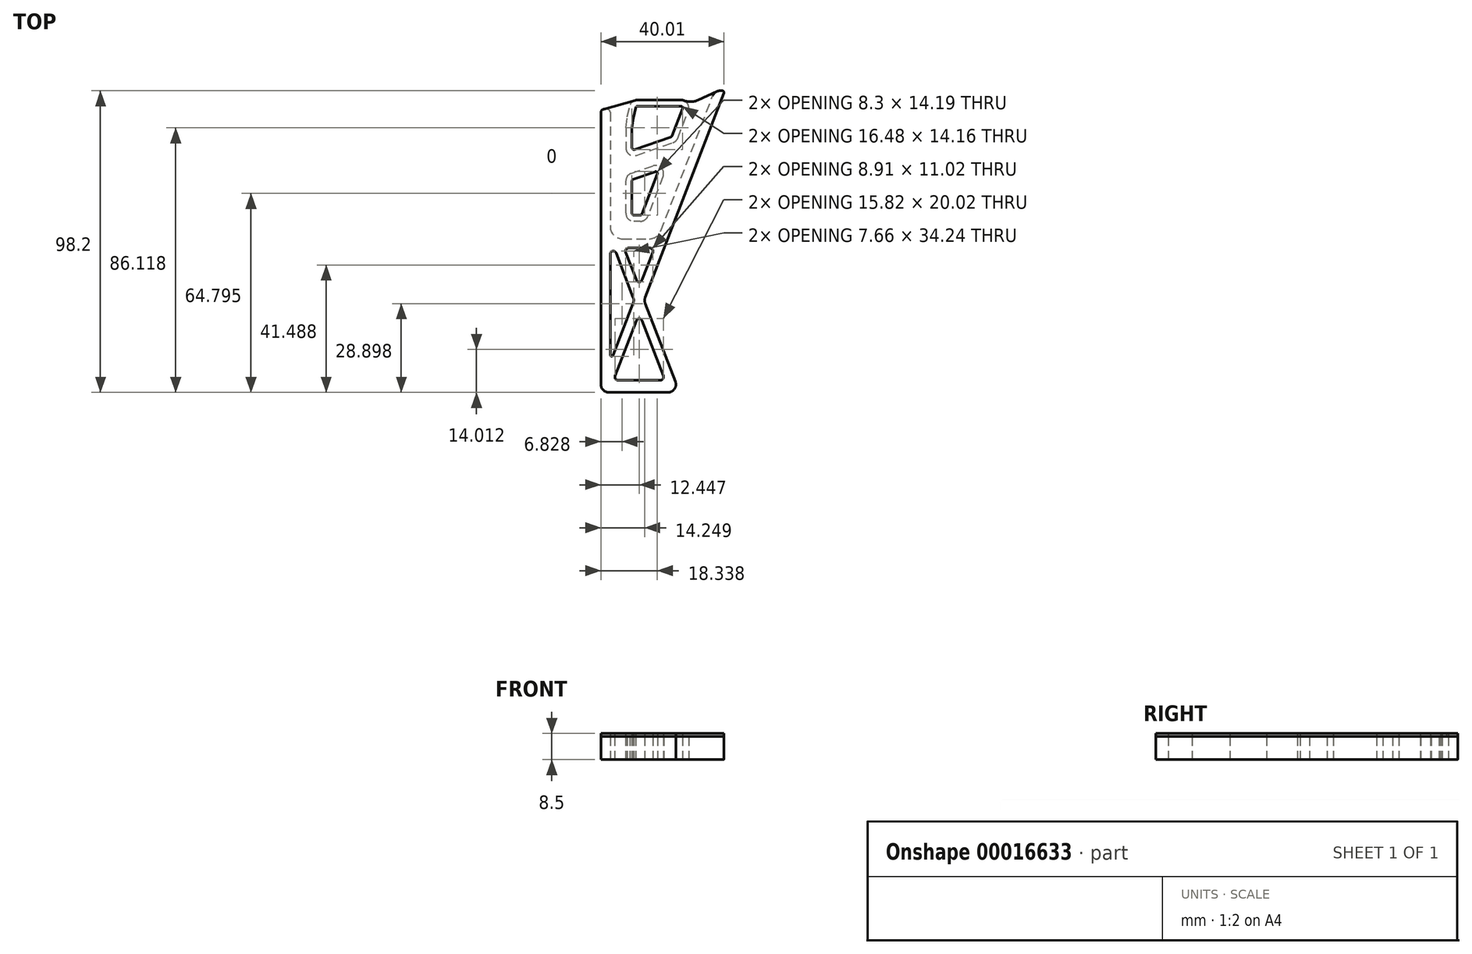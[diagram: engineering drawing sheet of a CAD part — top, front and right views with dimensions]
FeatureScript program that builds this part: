
annotation { "Feature Type Name" : "Feature", "Feature Type Description" : "" }
export const myFeature = defineFeature(function(context is Context, id is Id, definition is map)
    precondition{}
    {
        {
            var Q0;
            Q0=qCreatedBy(makeId("Top.planeOp"),FACE);
            var sketch = newSketch(context, id + "F0", { "sketchPlane" : qUnion([Q0])});
            skLineSegment(sketch, "E0", {"start": v(0, 2.6) * mm, "end": v(0, 13.15) * mm});
            skLineSegment(sketch, "E1", {"start": v(1.75, 15.6) * mm, "end": v(8.85, 18.05) * mm});
            skLineSegment(sketch, "E2", {"start": v(12.13, 14.66) * mm, "end": v(7.14, 1.67) * mm});
            skLineSegment(sketch, "E3", {"start": v(4.71, 0) * mm, "end": v(2.6, 0) * mm});
            skPoint(sketch, "E4.visualSharp", {"position": v(14.12, 19.86) * mm});
            skArc(sketch, "E4.filletArc", {"start": v(12.13, 14.66) * mm, "mid": v(11.57, 17.4) * mm, "end": v(8.85, 18.05) * mm});
            skPoint(sketch, "E5.visualSharp", {"position": v(0, 15) * mm});
            skArc(sketch, "E5.filletArc", {"start": v(1.75, 15.6) * mm, "mid": v(0.48, 14.66) * mm, "end": v(0, 13.15) * mm});
            skPoint(sketch, "E6.visualSharp", {"position": v(0, 0) * mm});
            skArc(sketch, "E6.filletArc", {"start": v(0, 2.6) * mm, "mid": v(0.76, 0.76) * mm, "end": v(2.6, 0) * mm});
            skPoint(sketch, "E7.visualSharp", {"position": v(6.5, 0) * mm});
            skArc(sketch, "E7.filletArc", {"start": v(4.71, 0) * mm, "mid": v(6.19, 0.46) * mm, "end": v(7.14, 1.67) * mm});
            skLineSegment(sketch, "E8", {"start": v(0, 30.5) * mm, "end": v(0, 23.93) * mm});
            skLineSegment(sketch, "E9", {"start": v(3.45, 21.47) * mm, "end": v(15.32, 25.56) * mm});
            skLineSegment(sketch, "E10", {"start": v(16.9, 27.09) * mm, "end": v(20.3, 35.97) * mm});
            skLineSegment(sketch, "E11", {"start": v(17.88, 39.5) * mm, "end": v(3.83, 39.5) * mm});
            skLineSegment(sketch, "E12", {"start": v(7.14, 1.67) * mm, "end": v(22.81, 42.5) * mm, "construction": true});
            skLineSegment(sketch, "E13", {"start": v(0, 2.6) * mm, "end": v(0, 43.18) * mm, "construction": true});
            skPoint(sketch, "E14.visualSharp", {"position": v(0, 20.29) * mm});
            skArc(sketch, "E14.filletArc", {"start": v(0, 23.93) * mm, "mid": v(1.1, 21.82) * mm, "end": v(3.45, 21.47) * mm});
            skPoint(sketch, "E15.visualSharp", {"position": v(16.46, 25.96) * mm});
            skArc(sketch, "E15.filletArc", {"start": v(15.32, 25.56) * mm, "mid": v(16.28, 26.15) * mm, "end": v(16.9, 27.09) * mm});
            skLineSegment(sketch, "E16", {"start": v(0, 30.5) * mm, "end": v(1.27, 37.37) * mm, "construction": true});
            skPoint(sketch, "E17.visualSharp", {"position": v(21.66, 39.5) * mm});
            skArc(sketch, "E17.filletArc", {"start": v(20.3, 35.97) * mm, "mid": v(20.02, 38.37) * mm, "end": v(17.88, 39.5) * mm});
            skPoint(sketch, "E18.visualSharp", {"position": v(1.66, 39.5) * mm});
            skArc(sketch, "E18.filletArc", {"start": v(3.83, 39.5) * mm, "mid": v(2.16, 38.9) * mm, "end": v(1.27, 37.37) * mm});
            skLineSegment(sketch, "E19", {"start": v(-5.1, 35.5) * mm, "end": v(-5.1, -1.7) * mm});
            skLineSegment(sketch, "E20", {"start": v(-1.1, -5.7) * mm, "end": v(7.67, -5.7) * mm});
            skLineSegment(sketch, "E21", {"start": v(11.4, -3.13) * mm, "end": v(28.28, 40.83) * mm});
            skLineSegment(sketch, "E22", {"start": v(-27.96, 39.5) * mm, "end": v(46.58, 39.5) * mm, "construction": true});
            skLineSegment(sketch, "E23", {"start": v(30.7, 42.5) * mm, "end": v(31.4, 42.5) * mm});
            skPoint(sketch, "E24.visualSharp", {"position": v(28.92, 42.5) * mm});
            skArc(sketch, "E24.filletArc", {"start": v(30.7, 42.5) * mm, "mid": v(29.23, 42.04) * mm, "end": v(28.28, 40.83) * mm});
            skLineSegment(sketch, "E25", {"start": v(-6.1, 36.5) * mm, "end": v(-7.1, 36.5) * mm});
            skLineSegment(sketch, "E26", {"start": v(-8.1, 35.5) * mm, "end": v(-8.1, -53.1) * mm});
            skLineSegment(sketch, "E27", {"start": v(6.31, -24.77) * mm, "end": v(31.87, 41.82) * mm});
            skPoint(sketch, "E28.visualSharp", {"position": v(-8.1, 36.5) * mm});
            skArc(sketch, "E28.filletArc", {"start": v(-7.1, 36.5) * mm, "mid": v(-7.8, 36.2) * mm, "end": v(-8.1, 35.5) * mm});
            skPoint(sketch, "E29.visualSharp", {"position": v(-5.1, 36.5) * mm});
            skArc(sketch, "E29.filletArc", {"start": v(-5.1, 35.5) * mm, "mid": v(-5.4, 36.2) * mm, "end": v(-6.1, 36.5) * mm});
            skPoint(sketch, "E30.visualSharp", {"position": v(32.13, 42.5) * mm});
            skArc(sketch, "E30.filletArc", {"start": v(31.87, 41.82) * mm, "mid": v(31.82, 42.28) * mm, "end": v(31.4, 42.5) * mm});
            skPoint(sketch, "E31.visualSharp", {"position": v(-5.1, -5.7) * mm});
            skArc(sketch, "E31.filletArc", {"start": v(-5.1, -1.7) * mm, "mid": v(-3.93, -4.53) * mm, "end": v(-1.1, -5.7) * mm});
            skPoint(sketch, "E32.visualSharp", {"position": v(10.42, -5.7) * mm});
            skArc(sketch, "E32.filletArc", {"start": v(7.67, -5.7) * mm, "mid": v(9.93, -5) * mm, "end": v(11.4, -3.13) * mm});
            skLineSegment(sketch, "E33", {"start": v(0, 30.5) * mm, "end": v(0.44, 33.97) * mm});
            skLineSegment(sketch, "E34", {"start": v(0.44, 33.97) * mm, "end": v(1.27, 37.37) * mm});
            skLineSegment(sketch, "E35", {"start": v(-31.23, -55.7) * mm, "end": v(37.12, -55.7) * mm, "construction": true});
            skLineSegment(sketch, "E36", {"start": v(16.11, -52.17) * mm, "end": v(6.31, -26.63) * mm});
            skLineSegment(sketch, "E37", {"start": v(13.69, -55.7) * mm, "end": v(-5.5, -55.7) * mm});
            skLineSegment(sketch, "E38", {"start": v(3.41, -32.32) * mm, "end": v(-3.5, -50.34) * mm});
            skLineSegment(sketch, "E39", {"start": v(-2.57, -51.7) * mm, "end": v(11.27, -51.7) * mm});
            skLineSegment(sketch, "E40", {"start": v(12.2, -50.34) * mm, "end": v(5.28, -32.32) * mm});
            skLineSegment(sketch, "E41", {"start": v(-0.05, -10.06) * mm, "end": v(3.41, -19.08) * mm});
            skLineSegment(sketch, "E42", {"start": v(5.28, -19.08) * mm, "end": v(8.74, -10.06) * mm});
            skLineSegment(sketch, "E43", {"start": v(7.81, -8.7) * mm, "end": v(0.88, -8.7) * mm});
            skLineSegment(sketch, "E44", {"start": v(5.95, -25.7) * mm, "end": v(-5.56, -55.7) * mm, "construction": true});
            skLineSegment(sketch, "E45", {"start": v(5.95, -25.7) * mm, "end": v(-6.5, 6.77) * mm, "construction": true});
            skLineSegment(sketch, "E46", {"start": v(-5.1, -10.67) * mm, "end": v(-5.1, -43.43) * mm});
            skLineSegment(sketch, "E47", {"start": v(-4.13, -43.6) * mm, "end": v(2.38, -26.63) * mm});
            skLineSegment(sketch, "E48", {"start": v(-3.17, -10.31) * mm, "end": v(2.38, -24.77) * mm});
            skPoint(sketch, "E49.visualSharp", {"position": v(17.47, -55.7) * mm});
            skArc(sketch, "E49.filletArc", {"start": v(13.69, -55.7) * mm, "mid": v(15.83, -54.57) * mm, "end": v(16.11, -52.17) * mm});
            skPoint(sketch, "E50.visualSharp", {"position": v(12.72, -51.7) * mm});
            skPoint(sketch, "E51.visualSharp", {"position": v(-4.03, -51.7) * mm});
            skPoint(sketch, "E52.visualSharp", {"position": v(4.35, -29.89) * mm});
            skPoint(sketch, "E53.visualSharp", {"position": v(-8.1, -55.7) * mm});
            skArc(sketch, "E53.filletArc", {"start": v(-8.1, -53.1) * mm, "mid": v(-7.34, -54.94) * mm, "end": v(-5.5, -55.7) * mm});
            skPoint(sketch, "E54.visualSharp", {"position": v(4.35, -21.51) * mm});
            skArc(sketch, "E54.filletArc", {"start": v(3.41, -19.08) * mm, "mid": v(4.35, -19.72) * mm, "end": v(5.28, -19.08) * mm});
            skPoint(sketch, "E55.visualSharp", {"position": v(9.27, -8.7) * mm});
            skArc(sketch, "E55.filletArc", {"start": v(8.74, -10.06) * mm, "mid": v(8.64, -9.13) * mm, "end": v(7.81, -8.7) * mm});
            skPoint(sketch, "E56.visualSharp", {"position": v(-0.57, -8.7) * mm});
            skArc(sketch, "E56.filletArc", {"start": v(0.88, -8.7) * mm, "mid": v(0.06, -9.13) * mm, "end": v(-0.05, -10.06) * mm});
            skArc(sketch, "E57", {"start": v(-3.17, -10.31) * mm, "mid": v(-4.28, -9.69) * mm, "end": v(-5.1, -10.67) * mm});
            skPoint(sketch, "E58.visualSharp", {"position": v(2.74, -25.7) * mm});
            skArc(sketch, "E58.filletArc", {"start": v(2.38, -26.63) * mm, "mid": v(2.56, -25.7) * mm, "end": v(2.38, -24.77) * mm});
            skPoint(sketch, "E59.visualSharp", {"position": v(5.95, -25.7) * mm});
            skArc(sketch, "E59.filletArc", {"start": v(6.31, -24.77) * mm, "mid": v(6.14, -25.7) * mm, "end": v(6.31, -26.63) * mm});
            skPoint(sketch, "E60.visualSharp", {"position": v(-5.1, -46.12) * mm});
            skArc(sketch, "E60.filletArc", {"start": v(-5.1, -43.43) * mm, "mid": v(-4.7, -43.92) * mm, "end": v(-4.13, -43.6) * mm});
            skArc(sketch, "E61.filletArc", {"start": v(-3.5, -50.34) * mm, "mid": v(-3.4, -51.27) * mm, "end": v(-2.57, -51.7) * mm});
            skArc(sketch, "E62.filletArc", {"start": v(11.27, -51.7) * mm, "mid": v(12.09, -51.27) * mm, "end": v(12.2, -50.34) * mm});
            skArc(sketch, "E63.filletArc", {"start": v(5.28, -32.32) * mm, "mid": v(4.35, -31.68) * mm, "end": v(3.41, -32.32) * mm});
            skSolve(sketch);
        }
        {
            var Q0;
            Q0 = qSketchRegion(id + "F0", true);
            extrude(context, id + "F1", {"entities" : qUnion([Q0]), "depth" : 7.5 * mm});
        }
        {
            var Q0;
            Q0=makeQuery(id+"F1.opExtrude","CAP_FACE",FACE,{"disambiguationData":[OSD([sQuery(id+"F0.wireOp",EDGE,"E8"),sQuery(id+"F0.wireOp",EDGE,"E9"),sQuery(id+"F0.wireOp",EDGE,"E10"),sQuery(id+"F0.wireOp",EDGE,"E11"),sQuery(id+"F0.wireOp",EDGE,"E14.filletArc"),sQuery(id+"F0.wireOp",EDGE,"E15.filletArc"),sQuery(id+"F0.wireOp",EDGE,"E16")])],"isStart":false});
            var Q1;
            Q1=makeQuery(id+"F1.opExtrude","CAP_FACE",FACE,{"disambiguationData":[OSD([sQuery(id+"F0.wireOp",EDGE,"E8"),sQuery(id+"F0.wireOp",EDGE,"E9"),sQuery(id+"F0.wireOp",EDGE,"E10"),sQuery(id+"F0.wireOp",EDGE,"E11"),sQuery(id+"F0.wireOp",EDGE,"E14.filletArc"),sQuery(id+"F0.wireOp",EDGE,"E15.filletArc"),sQuery(id+"F0.wireOp",EDGE,"E16")])],"isStart":true});
            var Q2;
            Q2=makeQuery(id+"F1.opExtrude","CAP_FACE",FACE,{"disambiguationData":[OSD([sQuery(id+"F0.wireOp",EDGE,"E0"),sQuery(id+"F0.wireOp",EDGE,"E1"),sQuery(id+"F0.wireOp",EDGE,"E2"),sQuery(id+"F0.wireOp",EDGE,"E3"),sQuery(id+"F0.wireOp",EDGE,"E4.filletArc"),sQuery(id+"F0.wireOp",EDGE,"E5.filletArc"),sQuery(id+"F0.wireOp",EDGE,"E6.filletArc"),sQuery(id+"F0.wireOp",EDGE,"E7.filletArc")])],"isStart":true});
            var Q3;
            Q3=makeQuery(id+"F1.opExtrude","CAP_FACE",FACE,{"disambiguationData":[OSD([sQuery(id+"F0.wireOp",EDGE,"E0"),sQuery(id+"F0.wireOp",EDGE,"E1"),sQuery(id+"F0.wireOp",EDGE,"E2"),sQuery(id+"F0.wireOp",EDGE,"E3"),sQuery(id+"F0.wireOp",EDGE,"E4.filletArc"),sQuery(id+"F0.wireOp",EDGE,"E5.filletArc"),sQuery(id+"F0.wireOp",EDGE,"E6.filletArc"),sQuery(id+"F0.wireOp",EDGE,"E7.filletArc")])],"isStart":false});
            shell(context, id + "F2", {"entities" : qUnion([Q0, Q1, Q2, Q3]), "thickness" : 2 * mm});
        }
        {
            var Q0;
            Q0=makeQuery(id+"F1.opExtrude","CAP_FACE",FACE,{"disambiguationData":[OSD([sQuery(id+"F0.wireOp",EDGE,"E19"),sQuery(id+"F0.wireOp",EDGE,"E20"),sQuery(id+"F0.wireOp",EDGE,"E21"),sQuery(id+"F0.wireOp",EDGE,"E23"),sQuery(id+"F0.wireOp",EDGE,"E24.filletArc"),sQuery(id+"F0.wireOp",EDGE,"E25"),sQuery(id+"F0.wireOp",EDGE,"E26"),sQuery(id+"F0.wireOp",EDGE,"E27"),sQuery(id+"F0.wireOp",EDGE,"E28.filletArc"),sQuery(id+"F0.wireOp",EDGE,"E29.filletArc"),sQuery(id+"F0.wireOp",EDGE,"E30.filletArc"),sQuery(id+"F0.wireOp",EDGE,"E31.filletArc"),sQuery(id+"F0.wireOp",EDGE,"E32.filletArc"),sQuery(id+"F0.wireOp",EDGE,"E36"),sQuery(id+"F0.wireOp",EDGE,"E37"),sQuery(id+"F0.wireOp",EDGE,"E38"),sQuery(id+"F0.wireOp",EDGE,"E39"),sQuery(id+"F0.wireOp",EDGE,"E40"),sQuery(id+"F0.wireOp",EDGE,"E41"),sQuery(id+"F0.wireOp",EDGE,"E42"),sQuery(id+"F0.wireOp",EDGE,"E43"),sQuery(id+"F0.wireOp",EDGE,"E46"),sQuery(id+"F0.wireOp",EDGE,"E47"),sQuery(id+"F0.wireOp",EDGE,"E48"),sQuery(id+"F0.wireOp",EDGE,"E49.filletArc"),sQuery(id+"F0.wireOp",EDGE,"E53.filletArc"),sQuery(id+"F0.wireOp",EDGE,"E54.filletArc"),sQuery(id+"F0.wireOp",EDGE,"E55.filletArc"),sQuery(id+"F0.wireOp",EDGE,"E56.filletArc"),sQuery(id+"F0.wireOp",EDGE,"E57"),sQuery(id+"F0.wireOp",EDGE,"E58.filletArc"),sQuery(id+"F0.wireOp",EDGE,"E59.filletArc"),sQuery(id+"F0.wireOp",EDGE,"E60.filletArc"),sQuery(id+"F0.wireOp",EDGE,"E61.filletArc"),sQuery(id+"F0.wireOp",EDGE,"E62.filletArc"),sQuery(id+"F0.wireOp",EDGE,"E63.filletArc")])],"isStart":true});
            var sketch = newSketch(context, id + "F3", { "sketchPlane" : qUnion([Q0])});
            skLineSegment(sketch, "E64.0", {"start": v(6.31, 24.77) * mm, "end": v(31.87, -41.82) * mm});
            skLineSegment(sketch, "E65.0", {"start": v(17.88, -39.5) * mm, "end": v(3.83, -39.5) * mm});
            skArc(sketch, "E66.0", {"start": v(-7.37, -36.46) * mm, "mid": v(-7.9, -36.1) * mm, "end": v(-8.1, -35.5) * mm});
            skArc(sketch, "E67.0", {"start": v(3.83, -39.5) * mm, "mid": v(3.47, -39.48) * mm, "end": v(3.12, -39.4) * mm});
            skArc(sketch, "E68.0", {"start": v(31.87, -41.82) * mm, "mid": v(31.82, -42.28) * mm, "end": v(31.4, -42.5) * mm});
            skLineSegment(sketch, "E69.0", {"start": v(30.7, -42.5) * mm, "end": v(31.4, -42.5) * mm});
            skArc(sketch, "E70.0", {"start": v(30.7, -42.5) * mm, "mid": v(30.4, -42.48) * mm, "end": v(30.1, -42.43) * mm});
            skArc(sketch, "E71.0.5", {"start": v(30.1, -42.43) * mm, "mid": v(30.4, -42.48) * mm, "end": v(30.7, -42.5) * mm});
            skArc(sketch, "E71.0.7", {"start": v(31.4, -42.5) * mm, "mid": v(31.82, -42.28) * mm, "end": v(31.87, -41.82) * mm});
            skLineSegment(sketch, "E71.0.8", {"start": v(31.87, -41.82) * mm, "end": v(6.31, 24.77) * mm});
            skArc(sketch, "E71.0.9", {"start": v(6.31, 24.77) * mm, "mid": v(6.14, 25.7) * mm, "end": v(6.31, 26.63) * mm});
            skLineSegment(sketch, "E71.0.10", {"start": v(6.31, 26.63) * mm, "end": v(16.11, 52.17) * mm});
            skArc(sketch, "E71.0.11", {"start": v(16.11, 52.17) * mm, "mid": v(15.83, 54.57) * mm, "end": v(13.69, 55.7) * mm});
            skLineSegment(sketch, "E71.0.12", {"start": v(13.69, 55.7) * mm, "end": v(-5.5, 55.7) * mm});
            skArc(sketch, "E71.0.13", {"start": v(-5.5, 55.7) * mm, "mid": v(-7.34, 54.94) * mm, "end": v(-8.1, 53.1) * mm});
            skArc(sketch, "E71.0.15", {"start": v(-8.1, -35.5) * mm, "mid": v(-7.9, -36.1) * mm, "end": v(-7.37, -36.46) * mm});
            skLineSegment(sketch, "E72.0", {"start": v(-5.1, 10.67) * mm, "end": v(-5.1, 43.43) * mm});
            skLineSegment(sketch, "E73.0", {"start": v(-3.17, 10.31) * mm, "end": v(2.38, 24.77) * mm});
            skArc(sketch, "E74.0", {"start": v(-3.17, 10.31) * mm, "mid": v(-4.28, 9.69) * mm, "end": v(-5.1, 10.67) * mm});
            skArc(sketch, "E75.0", {"start": v(0.88, 8.7) * mm, "mid": v(0.06, 9.13) * mm, "end": v(-0.05, 10.06) * mm});
            skLineSegment(sketch, "E76.0", {"start": v(7.81, 8.7) * mm, "end": v(0.88, 8.7) * mm});
            skArc(sketch, "E77.0", {"start": v(8.74, 10.06) * mm, "mid": v(8.64, 9.13) * mm, "end": v(7.81, 8.7) * mm});
            skLineSegment(sketch, "E78.0", {"start": v(5.28, 19.08) * mm, "end": v(8.74, 10.06) * mm});
            skLineSegment(sketch, "E79.0", {"start": v(-0.05, 10.06) * mm, "end": v(3.41, 19.08) * mm});
            skArc(sketch, "E80.0", {"start": v(3.41, 19.08) * mm, "mid": v(4.35, 19.72) * mm, "end": v(5.28, 19.08) * mm});
            skArc(sketch, "E81.0", {"start": v(2.38, 26.63) * mm, "mid": v(2.56, 25.7) * mm, "end": v(2.38, 24.77) * mm});
            skLineSegment(sketch, "E82.0", {"start": v(-4.13, 43.6) * mm, "end": v(2.38, 26.63) * mm});
            skArc(sketch, "E83.0", {"start": v(5.28, 32.32) * mm, "mid": v(4.35, 31.68) * mm, "end": v(3.41, 32.32) * mm});
            skLineSegment(sketch, "E84.0", {"start": v(3.41, 32.32) * mm, "end": v(-3.5, 50.34) * mm});
            skLineSegment(sketch, "E85.0", {"start": v(12.2, 50.34) * mm, "end": v(5.28, 32.32) * mm});
            skArc(sketch, "E86.0", {"start": v(-5.1, 43.43) * mm, "mid": v(-4.7, 43.92) * mm, "end": v(-4.13, 43.6) * mm});
            skArc(sketch, "E87.0", {"start": v(-3.5, 50.34) * mm, "mid": v(-3.4, 51.27) * mm, "end": v(-2.57, 51.7) * mm});
            skLineSegment(sketch, "E88.0", {"start": v(-2.57, 51.7) * mm, "end": v(11.27, 51.7) * mm});
            skArc(sketch, "E89.0", {"start": v(11.27, 51.7) * mm, "mid": v(12.09, 51.27) * mm, "end": v(12.2, 50.34) * mm});
            skLineSegment(sketch, "E90", {"start": v(30.1, -42.43) * mm, "end": v(17.88, -39.5) * mm});
            skPoint(sketch, "E91.orphan", {"position": v(28.28, -40.83) * mm});
            skLineSegment(sketch, "E92", {"start": v(3.12, -39.4) * mm, "end": v(-7.37, -36.46) * mm});
            skPoint(sketch, "E93.orphan", {"position": v(1.27, -37.37) * mm});
            skPoint(sketch, "E71.0.17.end.orphan", {"position": v(-5.1, -35.5) * mm});
            skPoint(sketch, "E71.0.16.end.orphan", {"position": v(-6.1, -36.5) * mm});
            skPoint(sketch, "E94.orphan", {"position": v(-7.1, -36.5) * mm});
            skLineSegment(sketch, "E95.0", {"start": v(-8.1, -35.5) * mm, "end": v(-8.1, 53.1) * mm});
            skLineSegment(sketch, "E96.0", {"start": v(2.8, -23.37) * mm, "end": v(14.67, -27.45) * mm});
            skLineSegment(sketch, "E97.0", {"start": v(15.03, -27.8) * mm, "end": v(18.44, -36.68) * mm});
            skLineSegment(sketch, "E98.0", {"start": v(10.26, -15.37) * mm, "end": v(5.27, -2.38) * mm});
            skLineSegment(sketch, "E99.0", {"start": v(2, -2.6) * mm, "end": v(2, -13.15) * mm});
            skArc(sketch, "E100.0", {"start": v(2, -2.6) * mm, "mid": v(2.18, -2.18) * mm, "end": v(2.6, -2) * mm});
            skLineSegment(sketch, "E101.0", {"start": v(4.71, -2) * mm, "end": v(2.6, -2) * mm});
            skArc(sketch, "E102.0", {"start": v(4.71, -2) * mm, "mid": v(5.05, -2.1) * mm, "end": v(5.27, -2.38) * mm});
            skLineSegment(sketch, "E103.0", {"start": v(2.4, -13.71) * mm, "end": v(9.5, -16.16) * mm});
            skArc(sketch, "E104.0", {"start": v(10.26, -15.37) * mm, "mid": v(10.13, -16) * mm, "end": v(9.5, -16.16) * mm});
            skArc(sketch, "E105.0", {"start": v(2.4, -13.71) * mm, "mid": v(2.11, -13.5) * mm, "end": v(2, -13.15) * mm});
            skArc(sketch, "E106.0", {"start": v(2, -23.93) * mm, "mid": v(2.25, -23.44) * mm, "end": v(2.8, -23.37) * mm});
            skLineSegment(sketch, "E107.0", {"start": v(2, -30.37) * mm, "end": v(2, -23.93) * mm});
            skArc(sketch, "E108.0", {"start": v(14.67, -27.45) * mm, "mid": v(14.89, -27.59) * mm, "end": v(15.03, -27.8) * mm});
            skLineSegment(sketch, "E109.0", {"start": v(17.88, -37.5) * mm, "end": v(3.83, -37.5) * mm});
            skArc(sketch, "E110.0", {"start": v(18.44, -36.68) * mm, "mid": v(18.37, -37.24) * mm, "end": v(17.88, -37.5) * mm});
            skLineSegment(sketch, "E111.0", {"start": v(2, -30.37) * mm, "end": v(2.4, -33.6) * mm});
            skLineSegment(sketch, "E112.0", {"start": v(2.4, -33.6) * mm, "end": v(3.23, -36.97) * mm});
            skArc(sketch, "E113.0", {"start": v(3.83, -37.5) * mm, "mid": v(3.43, -37.35) * mm, "end": v(3.23, -36.97) * mm});
            skSolve(sketch);
        }
        {
            var Q0;
            Q0=makeQuery(id+"F1.opExtrude","CAP_FACE",FACE,{"disambiguationData":[OSD([sQuery(id+"F0.wireOp",EDGE,"E19"),sQuery(id+"F0.wireOp",EDGE,"E20"),sQuery(id+"F0.wireOp",EDGE,"E21"),sQuery(id+"F0.wireOp",EDGE,"E23"),sQuery(id+"F0.wireOp",EDGE,"E24.filletArc"),sQuery(id+"F0.wireOp",EDGE,"E25"),sQuery(id+"F0.wireOp",EDGE,"E26"),sQuery(id+"F0.wireOp",EDGE,"E27"),sQuery(id+"F0.wireOp",EDGE,"E28.filletArc"),sQuery(id+"F0.wireOp",EDGE,"E29.filletArc"),sQuery(id+"F0.wireOp",EDGE,"E30.filletArc"),sQuery(id+"F0.wireOp",EDGE,"E31.filletArc"),sQuery(id+"F0.wireOp",EDGE,"E32.filletArc"),sQuery(id+"F0.wireOp",EDGE,"E36"),sQuery(id+"F0.wireOp",EDGE,"E37"),sQuery(id+"F0.wireOp",EDGE,"E38"),sQuery(id+"F0.wireOp",EDGE,"E39"),sQuery(id+"F0.wireOp",EDGE,"E40"),sQuery(id+"F0.wireOp",EDGE,"E41"),sQuery(id+"F0.wireOp",EDGE,"E42"),sQuery(id+"F0.wireOp",EDGE,"E43"),sQuery(id+"F0.wireOp",EDGE,"E46"),sQuery(id+"F0.wireOp",EDGE,"E47"),sQuery(id+"F0.wireOp",EDGE,"E48"),sQuery(id+"F0.wireOp",EDGE,"E49.filletArc"),sQuery(id+"F0.wireOp",EDGE,"E53.filletArc"),sQuery(id+"F0.wireOp",EDGE,"E54.filletArc"),sQuery(id+"F0.wireOp",EDGE,"E55.filletArc"),sQuery(id+"F0.wireOp",EDGE,"E56.filletArc"),sQuery(id+"F0.wireOp",EDGE,"E57"),sQuery(id+"F0.wireOp",EDGE,"E58.filletArc"),sQuery(id+"F0.wireOp",EDGE,"E59.filletArc"),sQuery(id+"F0.wireOp",EDGE,"E60.filletArc"),sQuery(id+"F0.wireOp",EDGE,"E61.filletArc"),sQuery(id+"F0.wireOp",EDGE,"E62.filletArc"),sQuery(id+"F0.wireOp",EDGE,"E63.filletArc")])],"isStart":false});
            var sketch = newSketch(context, id + "F4", { "sketchPlane" : qUnion([Q0])});
            skLineSegment(sketch, "E114.0", {"start": v(7.81, -8.7) * mm, "end": v(0.88, -8.7) * mm});
            skArc(sketch, "E115.0", {"start": v(0.88, -8.7) * mm, "mid": v(0.06, -9.13) * mm, "end": v(-0.05, -10.06) * mm});
            skLineSegment(sketch, "E116.0", {"start": v(-0.05, -10.06) * mm, "end": v(3.41, -19.08) * mm});
            skArc(sketch, "E117.0", {"start": v(3.41, -19.08) * mm, "mid": v(4.35, -19.72) * mm, "end": v(5.28, -19.08) * mm});
            skLineSegment(sketch, "E118.0", {"start": v(5.28, -19.08) * mm, "end": v(8.74, -10.06) * mm});
            skArc(sketch, "E119.0", {"start": v(8.74, -10.06) * mm, "mid": v(8.64, -9.13) * mm, "end": v(7.81, -8.7) * mm});
            skArc(sketch, "E120.0", {"start": v(-3.17, -10.31) * mm, "mid": v(-4.28, -9.69) * mm, "end": v(-5.1, -10.67) * mm});
            skLineSegment(sketch, "E121.0", {"start": v(-5.1, -10.67) * mm, "end": v(-5.1, -43.43) * mm});
            skLineSegment(sketch, "E122.0", {"start": v(-3.17, -10.31) * mm, "end": v(2.38, -24.77) * mm});
            skArc(sketch, "E123.0", {"start": v(2.38, -26.63) * mm, "mid": v(2.56, -25.7) * mm, "end": v(2.38, -24.77) * mm});
            skLineSegment(sketch, "E124.0", {"start": v(-4.13, -43.6) * mm, "end": v(2.38, -26.63) * mm});
            skArc(sketch, "E125.0", {"start": v(-5.1, -43.43) * mm, "mid": v(-4.7, -43.92) * mm, "end": v(-4.13, -43.6) * mm});
            skLineSegment(sketch, "E126.0", {"start": v(3.41, -32.32) * mm, "end": v(-3.5, -50.34) * mm});
            skLineSegment(sketch, "E127.0", {"start": v(-2.57, -51.7) * mm, "end": v(11.27, -51.7) * mm});
            skPoint(sketch, "E128.0", {"position": v(-3.4, -51.27) * mm});
            skLineSegment(sketch, "E129.0", {"start": v(12.2, -50.34) * mm, "end": v(5.28, -32.32) * mm});
            skArc(sketch, "E130.0", {"start": v(5.28, -32.32) * mm, "mid": v(4.35, -31.68) * mm, "end": v(3.41, -32.32) * mm});
            skArc(sketch, "E131.0", {"start": v(11.27, -51.7) * mm, "mid": v(12.09, -51.27) * mm, "end": v(12.2, -50.34) * mm});
            skArc(sketch, "E132.0", {"start": v(-3.5, -50.34) * mm, "mid": v(-3.4, -51.27) * mm, "end": v(-2.57, -51.7) * mm});
            skLineSegment(sketch, "E133.0", {"start": v(6.31, -24.77) * mm, "end": v(31.87, 41.82) * mm});
            skArc(sketch, "E134.0", {"start": v(6.31, -24.77) * mm, "mid": v(6.14, -25.7) * mm, "end": v(6.31, -26.63) * mm});
            skLineSegment(sketch, "E135.0", {"start": v(16.11, -52.17) * mm, "end": v(6.31, -26.63) * mm});
            skLineSegment(sketch, "E136.0", {"start": v(-8.1, 35.5) * mm, "end": v(-8.1, -53.1) * mm});
            skArc(sketch, "E137.0", {"start": v(13.69, -55.7) * mm, "mid": v(15.83, -54.57) * mm, "end": v(16.11, -52.17) * mm});
            skLineSegment(sketch, "E138.0", {"start": v(13.69, -55.7) * mm, "end": v(-5.5, -55.7) * mm});
            skArc(sketch, "E139.0", {"start": v(-8.1, -53.1) * mm, "mid": v(-7.34, -54.94) * mm, "end": v(-5.5, -55.7) * mm});
            skLineSegment(sketch, "E140.0", {"start": v(10.26, 15.37) * mm, "end": v(5.27, 2.38) * mm});
            skLineSegment(sketch, "E141.0", {"start": v(2.4, 13.71) * mm, "end": v(9.5, 16.16) * mm});
            skLineSegment(sketch, "E142.0", {"start": v(2, 2.6) * mm, "end": v(2, 13.15) * mm});
            skLineSegment(sketch, "E143.0", {"start": v(4.71, 2) * mm, "end": v(2.6, 2) * mm});
            skArc(sketch, "E144.0", {"start": v(4.71, 2) * mm, "mid": v(5.05, 2.1) * mm, "end": v(5.27, 2.38) * mm});
            skArc(sketch, "E145.0", {"start": v(2, 2.6) * mm, "mid": v(2.18, 2.18) * mm, "end": v(2.6, 2) * mm});
            skArc(sketch, "E146.0", {"start": v(10.26, 15.37) * mm, "mid": v(10.13, 16) * mm, "end": v(9.5, 16.16) * mm});
            skArc(sketch, "E147.0", {"start": v(2.4, 13.71) * mm, "mid": v(2.11, 13.5) * mm, "end": v(2, 13.15) * mm});
            skArc(sketch, "E148.0", {"start": v(3.83, 39.5) * mm, "mid": v(3.47, 39.48) * mm, "end": v(3.12, 39.4) * mm});
            skLineSegment(sketch, "E149.0", {"start": v(17.88, 39.5) * mm, "end": v(3.83, 39.5) * mm});
            skArc(sketch, "E150.0", {"start": v(-7.1, 36.5) * mm, "mid": v(-7.8, 36.2) * mm, "end": v(-8.1, 35.5) * mm});
            skArc(sketch, "E151.0", {"start": v(31.87, 41.82) * mm, "mid": v(31.82, 42.28) * mm, "end": v(31.4, 42.5) * mm});
            skLineSegment(sketch, "E152", {"start": v(-7.37, 36.46) * mm, "end": v(3.12, 39.4) * mm});
            skPoint(sketch, "E153.0.end.orphan", {"position": v(0.44, 33.97) * mm});
            skPoint(sketch, "E154.0.start.orphan", {"position": v(0, 30.5) * mm});
            skPoint(sketch, "E155.0.end.orphan", {"position": v(16.9, 27.09) * mm});
            skPoint(sketch, "E156.0.end.orphan", {"position": v(15.32, 25.56) * mm});
            skPoint(sketch, "E157.0.end.orphan", {"position": v(3.45, 21.47) * mm});
            skPoint(sketch, "E157.0.start.orphan", {"position": v(0, 23.93) * mm});
            skLineSegment(sketch, "E158.0", {"start": v(30.7, 42.5) * mm, "end": v(31.4, 42.5) * mm});
            skArc(sketch, "E159.0", {"start": v(30.7, 42.5) * mm, "mid": v(30.15, 42.44) * mm, "end": v(29.63, 42.27) * mm});
            skPoint(sketch, "E160.0.start.orphan", {"position": v(20.3, 35.97) * mm});
            skPoint(sketch, "E161.orphan", {"position": v(28.28, 40.83) * mm});
            skPoint(sketch, "E162.orphan", {"position": v(1.27, 37.37) * mm});
            skLineSegment(sketch, "E163.0", {"start": v(17.88, 37.5) * mm, "end": v(3.83, 37.5) * mm});
            skArc(sketch, "E164.0", {"start": v(18.44, 36.68) * mm, "mid": v(18.37, 37.24) * mm, "end": v(17.88, 37.5) * mm});
            skLineSegment(sketch, "E165.0", {"start": v(15.03, 27.8) * mm, "end": v(18.44, 36.68) * mm});
            skArc(sketch, "E166.0", {"start": v(14.67, 27.45) * mm, "mid": v(14.89, 27.59) * mm, "end": v(15.03, 27.8) * mm});
            skLineSegment(sketch, "E167.0", {"start": v(2.8, 23.37) * mm, "end": v(14.67, 27.45) * mm});
            skArc(sketch, "E168.0", {"start": v(2, 23.93) * mm, "mid": v(2.25, 23.44) * mm, "end": v(2.8, 23.37) * mm});
            skLineSegment(sketch, "E169.0", {"start": v(2, 30.37) * mm, "end": v(2, 23.93) * mm});
            skLineSegment(sketch, "E170.0", {"start": v(2, 30.37) * mm, "end": v(2.4, 33.6) * mm});
            skLineSegment(sketch, "E171.0", {"start": v(2.4, 33.6) * mm, "end": v(3.23, 36.97) * mm});
            skArc(sketch, "E172.0", {"start": v(3.83, 37.5) * mm, "mid": v(3.43, 37.35) * mm, "end": v(3.23, 36.97) * mm});
            skArc(sketch, "E173.trimOffspring", {"start": v(28.28, 40.83) * mm, "mid": v(28.27, 40.8) * mm, "end": v(28.26, 40.79) * mm});
            skArc(sketch, "E174.0", {"start": v(18.82, 39.32) * mm, "mid": v(18.36, 39.46) * mm, "end": v(17.88, 39.5) * mm});
            skLineSegment(sketch, "E175.trimOffspring", {"start": v(23.48, 39.46) * mm, "end": v(29.63, 42.27) * mm});
            skPoint(sketch, "E176.visualSharp", {"position": v(20.24, 37.98) * mm});
            skArc(sketch, "E176.filletArc", {"start": v(18.82, 39.32) * mm, "mid": v(21.17, 38.92) * mm, "end": v(23.48, 39.46) * mm});
            skSolve(sketch);
        }
        {
            var Q0;
            Q0 = qSketchRegion(id + "F4", true);
            extrude(context, id + "F5", {"entities" : qUnion([Q0]), "depth" : 1 * mm});
        }
    });
